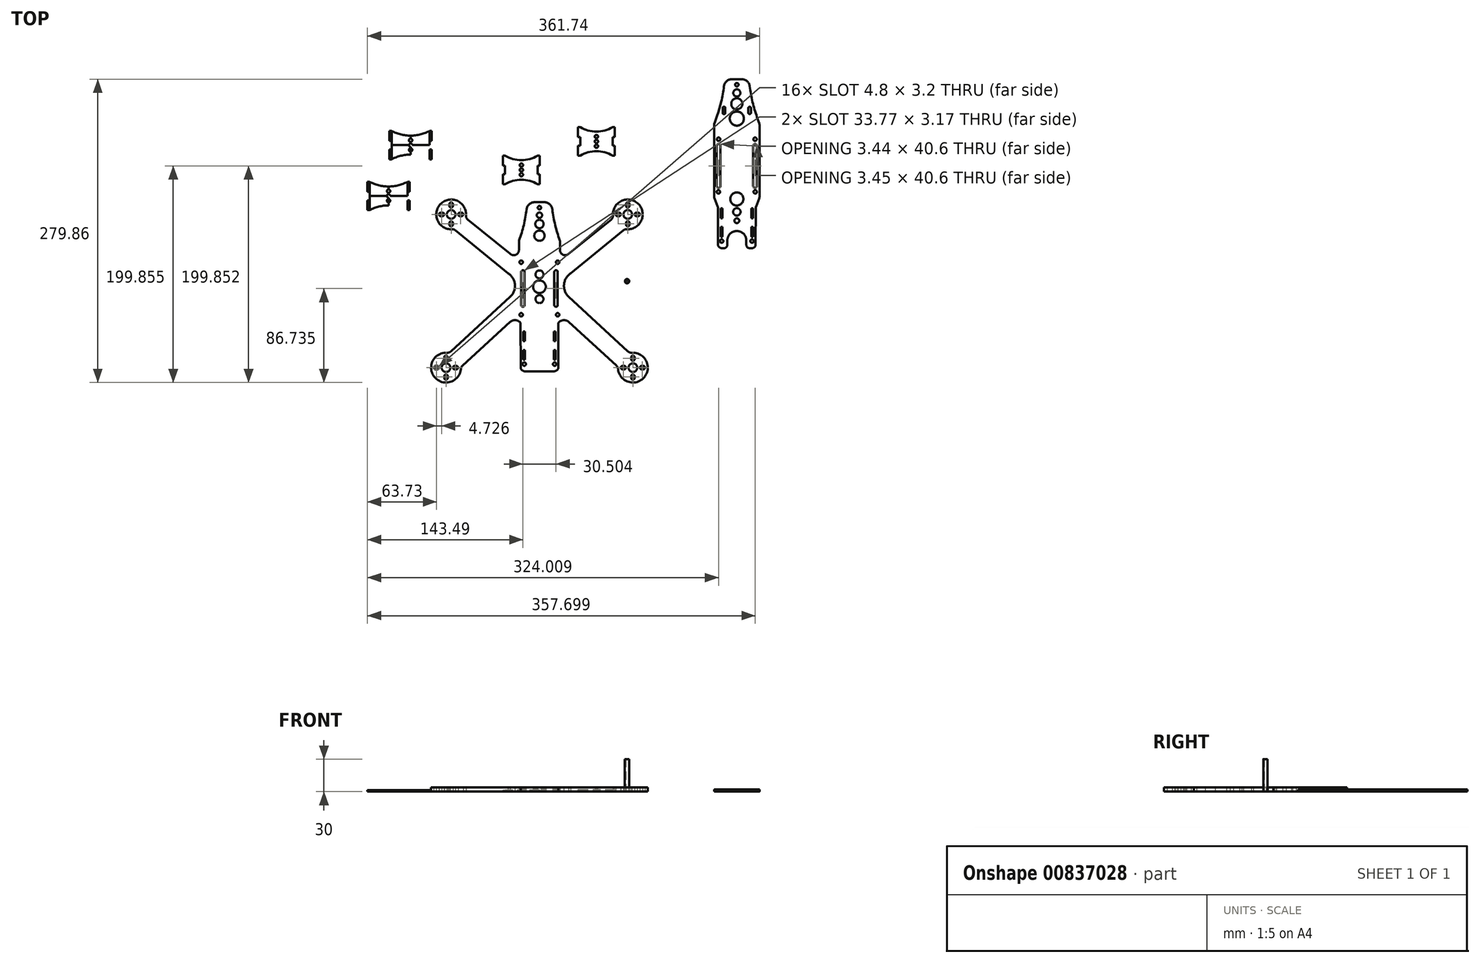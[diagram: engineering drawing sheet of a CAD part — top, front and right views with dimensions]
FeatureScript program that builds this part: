
annotation { "Feature Type Name" : "Feature", "Feature Type Description" : "" }
export const myFeature = defineFeature(function(context is Context, id is Id, definition is map)
    precondition{}
    {
        {
            var Q0;
            Q0=qCreatedBy(makeId("Top.planeOp"),FACE);
            var sketch = newSketch(context, id + "F0", { "sketchPlane" : qUnion([Q0])});
            skLineSegment(sketch, "E0.bottom", {"start": v(-59.9, 57.88) * mm, "end": v(-57.9, 57.88) * mm});
            skLineSegment(sketch, "E0.top", {"start": v(-59.9, 48.78) * mm, "end": v(-57.9, 48.78) * mm});
            skLineSegment(sketch, "E0.left", {"start": v(-59.9, 57.88) * mm, "end": v(-59.9, 48.78) * mm});
            skLineSegment(sketch, "E0.right", {"start": v(-57.9, 57.88) * mm, "end": v(-57.9, 48.78) * mm});
            skLineSegment(sketch, "E1", {"start": v(-57.9, 48.78) * mm, "end": v(-57.9, 40.77) * mm});
            skLineSegment(sketch, "E2.top", {"start": v(-59.9, 31.67) * mm, "end": v(-57.9, 31.67) * mm});
            skLineSegment(sketch, "E2.right", {"start": v(-57.9, 40.77) * mm, "end": v(-57.9, 31.67) * mm});
            skLineSegment(sketch, "E3.left", {"start": v(-57.9, 57.88) * mm, "end": v(-57.9, 31.68) * mm});
            skArc(sketch, "E4", {"start": v(-42.9, 50.83) * mm, "mid": v(-44.47, 49.27) * mm, "end": v(-42.9, 47.7) * mm});
            skArc(sketch, "E5", {"start": v(-42.9, 41.96) * mm, "mid": v(-44.47, 40.4) * mm, "end": v(-42.9, 38.84) * mm});
            skArc(sketch, "E6", {"start": v(-42.9, 46.34) * mm, "mid": v(-44.47, 44.78) * mm, "end": v(-42.9, 43.21) * mm});
            skLineSegment(sketch, "E7", {"start": v(-42.9, 53.68) * mm, "end": v(-42.9, 35.87) * mm});
            skPoint(sketch, "E3.right.end.orphan", {"position": v(-27.9, 31.68) * mm});
            skPoint(sketch, "E8.orphan", {"position": v(-27.9, 57.88) * mm});
            skPoint(sketch, "E9.0.midPoint", {"position": v(-51.12, 49.58) * mm});
            skPoint(sketch, "E10.0.midPoint", {"position": v(-51.12, 33.98) * mm});
            skPoint(sketch, "E11.0.midPoint", {"position": v(-50.1, 42.53) * mm});
            skLineSegment(sketch, "E12.MirrorCS", {"start": v(-27.9, 57.88) * mm, "end": v(-27.9, 48.78) * mm});
            skLineSegment(sketch, "E13.MirrorCS", {"start": v(-27.9, 40.77) * mm, "end": v(-27.9, 31.67) * mm});
            skLineSegment(sketch, "E14.MirrorCS", {"start": v(-27.9, 48.78) * mm, "end": v(-27.9, 40.77) * mm});
            skLineSegment(sketch, "E15.MirrorCS", {"start": v(-25.9, 40.77) * mm, "end": v(-25.9, 31.67) * mm});
            skLineSegment(sketch, "E16.MirrorCS", {"start": v(-25.9, 48.78) * mm, "end": v(-27.9, 48.78) * mm});
            skLineSegment(sketch, "E17.MirrorCS", {"start": v(-25.9, 57.88) * mm, "end": v(-25.9, 48.78) * mm});
            skLineSegment(sketch, "E18.MirrorCS", {"start": v(-27.9, 57.88) * mm, "end": v(-27.9, 31.68) * mm});
            skArc(sketch, "E19.MirrorCS", {"start": v(-42.9, 50.83) * mm, "mid": v(-41.34, 49.27) * mm, "end": v(-42.9, 47.7) * mm});
            skLineSegment(sketch, "E20.MirrorCS", {"start": v(-25.9, 31.67) * mm, "end": v(-27.9, 31.67) * mm});
            skLineSegment(sketch, "E21.MirrorCS", {"start": v(-25.9, 57.88) * mm, "end": v(-27.9, 57.88) * mm});
            skLineSegment(sketch, "E22.MirrorCS", {"start": v(-25.9, 40.77) * mm, "end": v(-27.9, 40.77) * mm});
            skArc(sketch, "E23.MirrorCS", {"start": v(-42.9, 46.34) * mm, "mid": v(-41.34, 44.78) * mm, "end": v(-42.9, 43.21) * mm});
            skArc(sketch, "E24.MirrorCS", {"start": v(-42.9, 41.96) * mm, "mid": v(-41.34, 40.4) * mm, "end": v(-42.9, 38.84) * mm});
            skLineSegment(sketch, "E25", {"start": v(-57.9, 40.77) * mm, "end": v(-59.9, 40.77) * mm});
            skLineSegment(sketch, "E26", {"start": v(-59.9, 40.77) * mm, "end": v(-59.9, 31.67) * mm});
            skLineSegment(sketch, "E27", {"start": v(-59.9, 31.67) * mm, "end": v(-57.9, 31.68) * mm});
            skPoint(sketch, "E28.orphan", {"position": v(-59.9, 31.67) * mm});
            skPoint(sketch, "E29.orphan", {"position": v(-42.9, 57.88) * mm});
            skPoint(sketch, "E30.orphan", {"position": v(-42.9, 31.68) * mm});
            skArc(sketch, "E31", {"start": v(-57.9, 57.88) * mm, "mid": v(-42.9, 53.84) * mm, "end": v(-27.9, 57.88) * mm});
            skLineSegment(sketch, "E32", {"start": v(-57.9, 44.78) * mm, "end": v(-27.9, 44.78) * mm});
            skArc(sketch, "E33.MirrorCS", {"start": v(-57.9, 31.68) * mm, "mid": v(-42.9, 35.71) * mm, "end": v(-27.9, 31.68) * mm});
            skSolve(sketch);
        }
        {
            var Q0;
            Q0=qCreatedBy(makeId("Top.planeOp"),FACE);
            var sketch = newSketch(context, id + "F1", { "sketchPlane" : qUnion([Q0])});
            skLineSegment(sketch, "E34.MirrorCS", {"start": v(0.83, -72.32) * mm, "end": v(55.44, -122.6) * mm});
            skLineSegment(sketch, "E35.MirrorCS", {"start": v(0.73, -95.48) * mm, "end": v(44.7, -135.8) * mm});
            skLineSegment(sketch, "E36.MirrorCS", {"start": v(2.74, -50.53) * mm, "end": v(51.32, -10.9) * mm});
            skLineSegment(sketch, "E37.MirrorCS", {"start": v(0.34, -32.94) * mm, "end": v(39.96, -0.95) * mm});
            skArc(sketch, "E38.MirrorCS", {"start": v(-21.66, 7.63) * mm, "mid": v(-21.66, 7.63) * mm, "end": v(-21.66, 7.63) * mm});
            skLineSegment(sketch, "E39", {"start": v(-26.23, 15) * mm, "end": v(-21.66, 15) * mm});
            skArc(sketch, "E40", {"start": v(-14.34, 8.5) * mm, "mid": v(-11.75, -6.01) * mm, "end": v(-7.5, -20.12) * mm});
            skArc(sketch, "E41.filletArc", {"start": v(-14.34, 8.5) * mm, "mid": v(-16.76, 13.14) * mm, "end": v(-21.66, 15) * mm});
            skPoint(sketch, "E42.MirrorP", {"position": v(-21.88, 15) * mm});
            skArc(sketch, "E43", {"start": v(-26.23, 8.41) * mm, "mid": v(-24.64, 10) * mm, "end": v(-26.23, 11.59) * mm});
            skArc(sketch, "E44", {"start": v(46.3, -138.99) * mm, "mid": v(70.46, -146.54) * mm, "end": v(59.14, -123.9) * mm});
            skPoint(sketch, "E45.visualSharp", {"position": v(41.88, 0.6) * mm});
            skPoint(sketch, "E46.visualSharp", {"position": v(-3.83, -55.9) * mm});
            skPoint(sketch, "E47.visualSharp", {"position": v(-3.86, -68) * mm});
            skPoint(sketch, "E48.visualSharp", {"position": v(57.16, -124.17) * mm});
            skArc(sketch, "E48.filletArc", {"start": v(55.44, -122.6) * mm, "mid": v(57.16, -123.63) * mm, "end": v(59.14, -123.9) * mm});
            skArc(sketch, "E49.filletArc", {"start": v(46.3, -138.99) * mm, "mid": v(45.8, -137.25) * mm, "end": v(44.7, -135.8) * mm});
            skLineSegment(sketch, "E50.MirrorCS", {"start": v(-26.23, 15) * mm, "end": v(-21.88, 15) * mm});
            skArc(sketch, "E51.MirrorCS", {"start": v(-30.58, 7.63) * mm, "mid": v(-30.58, 7.63) * mm, "end": v(-30.58, 7.63) * mm});
            skArc(sketch, "E52.MirrorC", {"start": v(-26.23, 11.59) * mm, "mid": v(-24.64, 10) * mm, "end": v(-26.23, 8.41) * mm});
            skPoint(sketch, "E53.MirrorP", {"position": v(-21.88, 7.63) * mm});
            skLineSegment(sketch, "E54", {"start": v(-26.23, -141) * mm, "end": v(-12.9, -141) * mm});
            skPoint(sketch, "E55.visualSharp", {"position": v(-4.15, -141) * mm});
            skCircle(sketch, "E56", {"center": v(-12.2, -134.36) * mm, "radius": 1.59 * mm});
            skPoint(sketch, "E57.visualSharp", {"position": v(-4.15, -91) * mm});
            skPoint(sketch, "E58.visualSharp", {"position": v(-3.84, -36.32) * mm});
            skArc(sketch, "E59", {"start": v(-9.4, -49.46) * mm, "mid": v(-10.98, -47.76) * mm, "end": v(-12.56, -49.46) * mm});
            skArc(sketch, "E60.MirrorC", {"start": v(-9.4, -79.95) * mm, "mid": v(-11.04, -81.53) * mm, "end": v(-12.56, -79.83) * mm});
            skLineSegment(sketch, "E61", {"start": v(-12.56, -49.23) * mm, "end": v(-12.56, -79.95) * mm});
            skLineSegment(sketch, "E62", {"start": v(-9.4, -49.23) * mm, "end": v(-9.4, -79.95) * mm});
            skPoint(sketch, "E63.endSnap0", {"position": v(-12.56, -64.59) * mm});
            skArc(sketch, "E64", {"start": v(54.34, -9.93) * mm, "mid": v(64.94, 13.55) * mm, "end": v(41.55, 2.74) * mm});
            skLineSegment(sketch, "E65.MirrorCS", {"start": v(93.25, 33.71) * mm, "end": v(93.25, 32.11) * mm});
            skLineSegment(sketch, "E66.MirrorCS", {"start": v(51.98, -136.03) * mm, "end": v(50.38, -136.03) * mm});
            skArc(sketch, "E67.MirrorCS", {"start": v(51.98, -136.03) * mm, "mid": v(53.58, -137.63) * mm, "end": v(51.98, -139.23) * mm});
            skArc(sketch, "E68.MirrorCS", {"start": v(50.38, -139.23) * mm, "mid": v(48.78, -137.63) * mm, "end": v(50.38, -136.03) * mm});
            skArc(sketch, "E69.MirrorCS", {"start": v(61.58, -129.73) * mm, "mid": v(59.98, -131.33) * mm, "end": v(58.38, -129.73) * mm});
            skLineSegment(sketch, "E70.MirrorCS", {"start": v(61.58, -128.13) * mm, "end": v(61.58, -129.73) * mm});
            skLineSegment(sketch, "E71.MirrorCS", {"start": v(58.38, -128.13) * mm, "end": v(58.38, -129.73) * mm});
            skArc(sketch, "E72.MirrorCS", {"start": v(58.38, -128.13) * mm, "mid": v(59.98, -126.53) * mm, "end": v(61.58, -128.13) * mm});
            skLineSegment(sketch, "E73.MirrorCS", {"start": v(51.98, -139.23) * mm, "end": v(50.38, -139.23) * mm});
            skArc(sketch, "E74.MirrorCS", {"start": v(58.38, -145.53) * mm, "mid": v(59.98, -143.93) * mm, "end": v(61.58, -145.53) * mm});
            skLineSegment(sketch, "E75.MirrorCS", {"start": v(58.38, -147.13) * mm, "end": v(58.38, -145.53) * mm});
            skArc(sketch, "E76.MirrorCS", {"start": v(61.58, -147.13) * mm, "mid": v(59.98, -148.73) * mm, "end": v(58.38, -147.13) * mm});
            skLineSegment(sketch, "E77.MirrorCS", {"start": v(61.58, -145.53) * mm, "end": v(61.58, -147.13) * mm});
            skCircle(sketch, "E78.MirrorC", {"center": v(59.98, -137.63) * mm, "radius": 4 * mm});
            skLineSegment(sketch, "E79.MirrorCS", {"start": v(69.58, -136.03) * mm, "end": v(67.98, -136.03) * mm});
            skArc(sketch, "E80.MirrorCS", {"start": v(67.98, -139.23) * mm, "mid": v(66.38, -137.63) * mm, "end": v(67.98, -136.03) * mm});
            skLineSegment(sketch, "E81.MirrorCS", {"start": v(67.98, -139.23) * mm, "end": v(69.58, -139.23) * mm});
            skArc(sketch, "E82.MirrorCS", {"start": v(69.58, -136.03) * mm, "mid": v(71.18, -137.63) * mm, "end": v(69.58, -139.23) * mm});
            skLineSegment(sketch, "E83.MirrorCS", {"start": v(47.26, 5.39) * mm, "end": v(45.66, 5.39) * mm});
            skArc(sketch, "E84.MirrorCS", {"start": v(47.26, 5.39) * mm, "mid": v(48.86, 3.79) * mm, "end": v(47.26, 2.19) * mm});
            skArc(sketch, "E85.MirrorCS", {"start": v(45.66, 2.19) * mm, "mid": v(44.06, 3.79) * mm, "end": v(45.66, 5.39) * mm});
            skArc(sketch, "E86.MirrorCS", {"start": v(56.86, 11.69) * mm, "mid": v(55.26, 10.09) * mm, "end": v(53.66, 11.69) * mm});
            skLineSegment(sketch, "E87.MirrorCS", {"start": v(56.86, 13.29) * mm, "end": v(56.86, 11.69) * mm});
            skLineSegment(sketch, "E88.MirrorCS", {"start": v(53.66, 13.29) * mm, "end": v(53.66, 11.69) * mm});
            skArc(sketch, "E89.MirrorCS", {"start": v(53.66, 13.29) * mm, "mid": v(55.26, 14.89) * mm, "end": v(56.86, 13.29) * mm});
            skLineSegment(sketch, "E90.MirrorCS", {"start": v(47.26, 2.19) * mm, "end": v(45.66, 2.19) * mm});
            skArc(sketch, "E91.MirrorCS", {"start": v(53.66, -4.11) * mm, "mid": v(55.26, -2.51) * mm, "end": v(56.86, -4.11) * mm});
            skLineSegment(sketch, "E92.MirrorCS", {"start": v(53.66, -5.71) * mm, "end": v(53.66, -4.11) * mm});
            skArc(sketch, "E93.MirrorCS", {"start": v(56.86, -5.71) * mm, "mid": v(55.26, -7.31) * mm, "end": v(53.66, -5.71) * mm});
            skLineSegment(sketch, "E94.MirrorCS", {"start": v(56.86, -4.11) * mm, "end": v(56.86, -5.71) * mm});
            skCircle(sketch, "E95.MirrorC", {"center": v(55.26, 3.79) * mm, "radius": 4 * mm});
            skLineSegment(sketch, "E96.MirrorCS", {"start": v(64.86, 5.39) * mm, "end": v(63.26, 5.39) * mm});
            skArc(sketch, "E97.MirrorCS", {"start": v(63.26, 2.19) * mm, "mid": v(61.66, 3.79) * mm, "end": v(63.26, 5.39) * mm});
            skLineSegment(sketch, "E98.MirrorCS", {"start": v(63.26, 2.19) * mm, "end": v(64.86, 2.19) * mm});
            skArc(sketch, "E99.MirrorCS", {"start": v(64.86, 5.39) * mm, "mid": v(66.46, 3.79) * mm, "end": v(64.86, 2.19) * mm});
            skPoint(sketch, "E100.orphan", {"position": v(-4.2, -107.89) * mm});
            skPoint(sketch, "E101.visualSharp", {"position": v(-10.15, -141) * mm});
            skArc(sketch, "E101.filletArc", {"start": v(-12.9, -141) * mm, "mid": v(-10.54, -140.3) * mm, "end": v(-8.94, -138.43) * mm});
            skPoint(sketch, "E102.visualSharp", {"position": v(52.75, -9.73) * mm});
            skArc(sketch, "E102.filletArc", {"start": v(54.34, -9.93) * mm, "mid": v(52.74, -10.13) * mm, "end": v(51.32, -10.9) * mm});
            skArc(sketch, "E103.filletArc", {"start": v(39.96, -0.95) * mm, "mid": v(41.2, 0.7) * mm, "end": v(41.55, 2.74) * mm});
            skLineSegment(sketch, "E104", {"start": v(-8.73, -96.45) * mm, "end": v(-8.94, -138.43) * mm});
            skArc(sketch, "E105", {"start": v(0.73, -95.48) * mm, "mid": v(-4.13, -93.82) * mm, "end": v(-8.66, -96.25) * mm});
            skLineSegment(sketch, "E106", {"start": v(-7.31, -21.23) * mm, "end": v(-7.31, -29.47) * mm});
            skPoint(sketch, "E107.orphan", {"position": v(-3.73, -29.32) * mm});
            skPoint(sketch, "E108.visualSharp", {"position": v(-7.31, -34.27) * mm});
            skPoint(sketch, "E109.visualSharp", {"position": v(-1.3, -34.27) * mm});
            skPoint(sketch, "E110.MirrorCS.end.orphan", {"position": v(-12.56, -87.45) * mm});
            skPoint(sketch, "E110.MirrorCS.start.orphan", {"position": v(-12.56, -79.83) * mm});
            skPoint(sketch, "E111.visualSharp", {"position": v(1.83, -51.27) * mm});
            skPoint(sketch, "E112.visualSharp", {"position": v(-7.31, -20.65) * mm});
            skArc(sketch, "E112.filletArc", {"start": v(-7.31, -21.23) * mm, "mid": v(-7.36, -20.67) * mm, "end": v(-7.5, -20.12) * mm});
            skArc(sketch, "E113.MirrorCS", {"start": v(0.83, -72.32) * mm, "mid": v(-3.57, -60.95) * mm, "end": v(2.74, -50.53) * mm});
            skCircle(sketch, "E114.MirrorC", {"center": v(-9.4, -88.84) * mm, "radius": 1.59 * mm});
            skCircle(sketch, "E115.MirrorC", {"center": v(-9.4, -40.34) * mm, "radius": 1.59 * mm});
            skArc(sketch, "E116", {"start": v(-26.23, -55.28) * mm, "mid": v(-22.54, -51.6) * mm, "end": v(-26.23, -47.91) * mm});
            skArc(sketch, "E117", {"start": v(-26.23, -68.87) * mm, "mid": v(-20.36, -63) * mm, "end": v(-26.23, -57.13) * mm});
            skArc(sketch, "E118.MirrorC", {"start": v(-26.23, -70.72) * mm, "mid": v(-22.54, -74.4) * mm, "end": v(-26.23, -78.09) * mm});
            skPoint(sketch, "E119.visualSharp", {"position": v(-23.79, 5.4) * mm});
            skArc(sketch, "E120", {"start": v(-26.23, 0.55) * mm, "mid": v(-23.74, 3.04) * mm, "end": v(-26.23, 5.52) * mm});
            skArc(sketch, "E121", {"start": v(-26.23, -9) * mm, "mid": v(-22.35, -5.11) * mm, "end": v(-26.23, -1.23) * mm});
            skArc(sketch, "E122", {"start": v(-26.23, -20.63) * mm, "mid": v(-21.47, -15.87) * mm, "end": v(-26.23, -11.12) * mm});
            skArc(sketch, "E123", {"start": v(-7.31, -29.47) * mm, "mid": v(-4.29, -33.53) * mm, "end": v(0.7, -32.65) * mm});
            skLineSegment(sketch, "E124.MirrorCS", {"start": v(-99.71, 2.19) * mm, "end": v(-98.11, 2.19) * mm});
            skLineSegment(sketch, "E125.MirrorCS", {"start": v(-99.71, 5.39) * mm, "end": v(-98.11, 5.39) * mm});
            skArc(sketch, "E126.MirrorCS", {"start": v(-92.41, -0.95) * mm, "mid": v(-93.66, 0.7) * mm, "end": v(-94, 2.74) * mm});
            skArc(sketch, "E127.MirrorCS", {"start": v(-98.11, 2.19) * mm, "mid": v(-96.51, 3.79) * mm, "end": v(-98.11, 5.39) * mm});
            skLineSegment(sketch, "E128.MirrorCS", {"start": v(-106.11, -5.71) * mm, "end": v(-106.11, -4.11) * mm});
            skArc(sketch, "E129.MirrorCS", {"start": v(-99.71, 5.39) * mm, "mid": v(-101.31, 3.79) * mm, "end": v(-99.71, 2.19) * mm});
            skLineSegment(sketch, "E130.MirrorCS", {"start": v(-110.84, -128.13) * mm, "end": v(-110.84, -129.73) * mm});
            skLineSegment(sketch, "E131.MirrorCS", {"start": v(-41.1, -130.4) * mm, "end": v(-39.5, -130.4) * mm});
            skArc(sketch, "E132.MirrorCS", {"start": v(-114.04, -129.73) * mm, "mid": v(-112.44, -131.33) * mm, "end": v(-110.84, -129.73) * mm});
            skLineSegment(sketch, "E133.MirrorCS", {"start": v(-26.23, 15) * mm, "end": v(-30.8, 15) * mm});
            skLineSegment(sketch, "E134.MirrorCS", {"start": v(-122.04, -136.03) * mm, "end": v(-120.44, -136.03) * mm});
            skArc(sketch, "E135.MirrorCS", {"start": v(-110.84, -128.13) * mm, "mid": v(-112.44, -126.53) * mm, "end": v(-114.04, -128.13) * mm});
            skLineSegment(sketch, "E136.MirrorCS", {"start": v(-109.31, -4.11) * mm, "end": v(-109.31, -5.71) * mm});
            skArc(sketch, "E137.MirrorCS", {"start": v(-26.23, 11.59) * mm, "mid": v(-27.81, 10) * mm, "end": v(-26.23, 8.41) * mm});
            skArc(sketch, "E138.MirrorCS", {"start": v(-107.9, -122.6) * mm, "mid": v(-109.61, -123.63) * mm, "end": v(-111.6, -123.9) * mm});
            skLineSegment(sketch, "E139.MirrorCS", {"start": v(-115.71, 2.19) * mm, "end": v(-117.31, 2.19) * mm});
            skLineSegment(sketch, "E140.MirrorCS", {"start": v(-117.31, 5.39) * mm, "end": v(-115.71, 5.39) * mm});
            skLineSegment(sketch, "E141.MirrorCS", {"start": v(-114.04, -128.13) * mm, "end": v(-114.04, -129.73) * mm});
            skArc(sketch, "E142.MirrorCS", {"start": v(-106.11, -4.11) * mm, "mid": v(-107.71, -2.51) * mm, "end": v(-109.31, -4.11) * mm});
            skCircle(sketch, "E143.MirrorC", {"center": v(-40.25, -134.36) * mm, "radius": 1.59 * mm});
            skArc(sketch, "E144.MirrorCS", {"start": v(-115.71, 2.19) * mm, "mid": v(-114.11, 3.79) * mm, "end": v(-115.71, 5.39) * mm});
            skLineSegment(sketch, "E145.MirrorCS", {"start": v(-114.04, -145.53) * mm, "end": v(-114.04, -147.13) * mm});
            skArc(sketch, "E146.MirrorCS", {"start": v(-120.44, -139.23) * mm, "mid": v(-118.84, -137.63) * mm, "end": v(-120.44, -136.03) * mm});
            skLineSegment(sketch, "E147.MirrorCS", {"start": v(-41.1, -113.28) * mm, "end": v(-41.1, -104.16) * mm});
            skArc(sketch, "E148.MirrorCS", {"start": v(-26.23, 8.41) * mm, "mid": v(-27.81, 10) * mm, "end": v(-26.23, 11.59) * mm});
            skArc(sketch, "E149.MirrorCS", {"start": v(-104.44, -136.03) * mm, "mid": v(-106.04, -137.63) * mm, "end": v(-104.44, -139.23) * mm});
            skLineSegment(sketch, "E150.MirrorCS", {"start": v(-41.1, -121.28) * mm, "end": v(-39.5, -121.28) * mm});
            skLineSegment(sketch, "E151.MirrorCS", {"start": v(-26.23, 15) * mm, "end": v(-30.58, 15) * mm});
            skLineSegment(sketch, "E152.MirrorCS", {"start": v(-41.1, -121.28) * mm, "end": v(-41.1, -130.4) * mm});
            skArc(sketch, "E153.MirrorCS", {"start": v(-114.04, -147.13) * mm, "mid": v(-112.44, -148.73) * mm, "end": v(-110.84, -147.13) * mm});
            skArc(sketch, "E154.MirrorCS", {"start": v(-30.8, 7.63) * mm, "mid": v(-30.8, 7.63) * mm, "end": v(-30.8, 7.63) * mm});
            skLineSegment(sketch, "E155.MirrorCS", {"start": v(-110.84, -147.13) * mm, "end": v(-110.84, -145.53) * mm});
            skArc(sketch, "E156.MirrorCS", {"start": v(-21.88, 7.63) * mm, "mid": v(-21.88, 7.63) * mm, "end": v(-21.88, 7.63) * mm});
            skLineSegment(sketch, "E157.MirrorCS", {"start": v(-41.1, -113.28) * mm, "end": v(-39.5, -113.28) * mm});
            skArc(sketch, "E158.MirrorCS", {"start": v(-38.12, 8.5) * mm, "mid": v(-35.7, 13.14) * mm, "end": v(-30.8, 15) * mm});
            skLineSegment(sketch, "E159.MirrorCS", {"start": v(-39.5, -121.28) * mm, "end": v(-39.5, -130.4) * mm});
            skCircle(sketch, "E160.MirrorC", {"center": v(-112.44, -137.63) * mm, "radius": 4 * mm});
            skArc(sketch, "E161.MirrorCS", {"start": v(-110.84, -145.53) * mm, "mid": v(-112.44, -143.93) * mm, "end": v(-114.04, -145.53) * mm});
            skArc(sketch, "E162.MirrorCS", {"start": v(-45.14, -21.23) * mm, "mid": v(-45.1, -20.67) * mm, "end": v(-44.95, -20.12) * mm});
            skCircle(sketch, "E163.MirrorC", {"center": v(-107.71, 3.79) * mm, "radius": 4 * mm});
            skLineSegment(sketch, "E164.MirrorCS", {"start": v(-120.44, -139.23) * mm, "end": v(-122.04, -139.23) * mm});
            skLineSegment(sketch, "E165.MirrorCS", {"start": v(-104.44, -136.03) * mm, "end": v(-102.84, -136.03) * mm});
            skArc(sketch, "E166.MirrorCS", {"start": v(-117.31, 5.39) * mm, "mid": v(-118.91, 3.79) * mm, "end": v(-117.31, 2.19) * mm});
            skArc(sketch, "E167.MirrorCS", {"start": v(-102.84, -139.23) * mm, "mid": v(-101.24, -137.63) * mm, "end": v(-102.84, -136.03) * mm});
            skLineSegment(sketch, "E168.MirrorCS", {"start": v(-39.5, -113.28) * mm, "end": v(-39.5, -104.16) * mm});
            skLineSegment(sketch, "E169.MirrorCS", {"start": v(-109.31, 13.29) * mm, "end": v(-109.31, 11.69) * mm});
            skLineSegment(sketch, "E170.MirrorCS", {"start": v(-104.44, -139.23) * mm, "end": v(-102.84, -139.23) * mm});
            skLineSegment(sketch, "E171.MirrorCS", {"start": v(-43.73, -96.45) * mm, "end": v(-43.51, -138.43) * mm});
            skArc(sketch, "E172.MirrorCS", {"start": v(-98.76, -138.99) * mm, "mid": v(-98.25, -137.25) * mm, "end": v(-97.16, -135.8) * mm});
            skArc(sketch, "E173.MirrorCS", {"start": v(-109.31, 11.69) * mm, "mid": v(-107.71, 10.09) * mm, "end": v(-106.11, 11.69) * mm});
            skArc(sketch, "E174.MirrorCS", {"start": v(-26.23, 0.55) * mm, "mid": v(-28.71, 3.04) * mm, "end": v(-26.23, 5.52) * mm});
            skLineSegment(sketch, "E175.MirrorCS", {"start": v(-41.1, -104.16) * mm, "end": v(-39.5, -104.16) * mm});
            skArc(sketch, "E176.MirrorCS", {"start": v(-43.06, -49.46) * mm, "mid": v(-41.48, -47.76) * mm, "end": v(-39.9, -49.46) * mm});
            skArc(sketch, "E177.MirrorCS", {"start": v(-26.23, -9) * mm, "mid": v(-30.1, -5.11) * mm, "end": v(-26.23, -1.23) * mm});
            skArc(sketch, "E178.MirrorCS", {"start": v(-43.06, -79.95) * mm, "mid": v(-41.42, -81.53) * mm, "end": v(-39.9, -79.83) * mm});
            skArc(sketch, "E179.MirrorCS", {"start": v(-109.31, -5.71) * mm, "mid": v(-107.71, -7.31) * mm, "end": v(-106.11, -5.71) * mm});
            skArc(sketch, "E180.MirrorCS", {"start": v(-45.14, -29.47) * mm, "mid": v(-48.17, -33.53) * mm, "end": v(-53.16, -32.65) * mm});
            skArc(sketch, "E181.MirrorCS", {"start": v(-39.56, -141) * mm, "mid": v(-41.92, -140.3) * mm, "end": v(-43.51, -138.43) * mm});
            skArc(sketch, "E182.MirrorCS", {"start": v(-106.11, 13.29) * mm, "mid": v(-107.71, 14.89) * mm, "end": v(-109.31, 13.29) * mm});
            skLineSegment(sketch, "E183.MirrorCS", {"start": v(-106.11, 13.29) * mm, "end": v(-106.11, 11.69) * mm});
            skLineSegment(sketch, "E184.MirrorCS", {"start": v(-45.14, -21.23) * mm, "end": v(-45.14, -29.47) * mm});
            skLineSegment(sketch, "E185.MirrorCS", {"start": v(-26.23, -141) * mm, "end": v(-39.56, -141) * mm});
            skArc(sketch, "E186.MirrorCS", {"start": v(-106.8, -9.93) * mm, "mid": v(-105.2, -10.13) * mm, "end": v(-103.78, -10.9) * mm});
            skCircle(sketch, "E187.MirrorC", {"center": v(-43.06, -88.84) * mm, "radius": 1.59 * mm});
            skArc(sketch, "E188.MirrorCS", {"start": v(-98.76, -138.99) * mm, "mid": v(-122.91, -146.54) * mm, "end": v(-111.6, -123.9) * mm});
            skArc(sketch, "E189.MirrorCS", {"start": v(-122.04, -136.03) * mm, "mid": v(-123.64, -137.63) * mm, "end": v(-122.04, -139.23) * mm});
            skArc(sketch, "E190.MirrorCS", {"start": v(-26.23, -55.28) * mm, "mid": v(-29.91, -51.6) * mm, "end": v(-26.23, -47.91) * mm});
            skCircle(sketch, "E191.MirrorC", {"center": v(-43.06, -40.34) * mm, "radius": 1.59 * mm});
            skArc(sketch, "E192.MirrorCS", {"start": v(-26.23, -70.72) * mm, "mid": v(-29.91, -74.4) * mm, "end": v(-26.23, -78.09) * mm});
            skArc(sketch, "E193.MirrorCS", {"start": v(-26.23, -68.87) * mm, "mid": v(-32.1, -63) * mm, "end": v(-26.23, -57.13) * mm});
            skPoint(sketch, "E194.MirrorP", {"position": v(-30.58, 15) * mm});
            skArc(sketch, "E195.MirrorCS", {"start": v(-53.19, -95.48) * mm, "mid": v(-48.33, -93.82) * mm, "end": v(-43.8, -96.25) * mm});
            skPoint(sketch, "E196.MirrorP", {"position": v(-94.34, 0.6) * mm});
            skArc(sketch, "E197.MirrorCS", {"start": v(-26.23, -20.63) * mm, "mid": v(-30.98, -15.87) * mm, "end": v(-26.23, -11.12) * mm});
            skPoint(sketch, "E198.MirrorP", {"position": v(-42.3, -141) * mm});
            skPoint(sketch, "E199.MirrorP", {"position": v(-48.3, -141) * mm});
            skArc(sketch, "E200.MirrorCS", {"start": v(-53.29, -72.32) * mm, "mid": v(-48.88, -60.95) * mm, "end": v(-55.2, -50.53) * mm});
            skPoint(sketch, "E201.MirrorP", {"position": v(-30.58, 7.63) * mm});
            skPoint(sketch, "E202.MirrorP", {"position": v(-45.14, -20.65) * mm});
            skArc(sketch, "E203.MirrorCS", {"start": v(-38.12, 8.5) * mm, "mid": v(-40.7, -6.01) * mm, "end": v(-44.95, -20.12) * mm});
            skLineSegment(sketch, "E204.MirrorCS", {"start": v(-43.06, -49.23) * mm, "end": v(-43.06, -79.95) * mm});
            skLineSegment(sketch, "E205.MirrorCS", {"start": v(-39.9, -49.23) * mm, "end": v(-39.9, -79.95) * mm});
            skPoint(sketch, "E206.MirrorP", {"position": v(-48.73, -29.32) * mm});
            skPoint(sketch, "E207.MirrorP", {"position": v(-28.67, 5.4) * mm});
            skPoint(sketch, "E208.MirrorP", {"position": v(-51.15, -34.27) * mm});
            skLineSegment(sketch, "E209.MirrorCS", {"start": v(-55.2, -50.53) * mm, "end": v(-103.78, -10.9) * mm});
            skPoint(sketch, "E210.MirrorP", {"position": v(-105.2, -9.73) * mm});
            skPoint(sketch, "E211.MirrorP", {"position": v(-39.9, -64.59) * mm});
            skPoint(sketch, "E212.MirrorP", {"position": v(-54.28, -51.27) * mm});
            skPoint(sketch, "E213.MirrorP", {"position": v(-48.61, -36.32) * mm});
            skPoint(sketch, "E214.MirrorP", {"position": v(-45.14, -34.27) * mm});
            skLineSegment(sketch, "E215.MirrorCS", {"start": v(-53.19, -95.48) * mm, "end": v(-97.16, -135.8) * mm});
            skLineSegment(sketch, "E216.MirrorCS", {"start": v(-53.29, -72.32) * mm, "end": v(-107.9, -122.6) * mm});
            skPoint(sketch, "E217.MirrorP", {"position": v(-48.25, -107.89) * mm});
            skArc(sketch, "E218.MirrorCS", {"start": v(-106.8, -9.93) * mm, "mid": v(-117.4, 13.55) * mm, "end": v(-94, 2.74) * mm});
            skPoint(sketch, "E219.MirrorP", {"position": v(-48.6, -68) * mm});
            skPoint(sketch, "E220.MirrorP", {"position": v(-48.3, -91) * mm});
            skPoint(sketch, "E221.MirrorP", {"position": v(-48.63, -55.9) * mm});
            skPoint(sketch, "E222.MirrorP", {"position": v(-39.9, -79.83) * mm});
            skPoint(sketch, "E223.MirrorP", {"position": v(-39.9, -87.45) * mm});
            skLineSegment(sketch, "E224.MirrorCS", {"start": v(-52.8, -32.94) * mm, "end": v(-92.41, -0.95) * mm});
            skPoint(sketch, "E225.MirrorP", {"position": v(-109.61, -124.17) * mm});
            skLineSegment(sketch, "E226.MirrorCS", {"start": v(-11.36, -113.28) * mm, "end": v(-12.96, -113.28) * mm});
            skLineSegment(sketch, "E227.MirrorCS", {"start": v(-11.36, -130.4) * mm, "end": v(-12.96, -130.4) * mm});
            skLineSegment(sketch, "E228.MirrorCS", {"start": v(-11.36, -121.28) * mm, "end": v(-12.96, -121.28) * mm});
            skLineSegment(sketch, "E229.MirrorCS", {"start": v(-11.36, -104.16) * mm, "end": v(-12.96, -104.16) * mm});
            skLineSegment(sketch, "E230.MirrorCS", {"start": v(-12.96, -121.28) * mm, "end": v(-12.96, -130.4) * mm});
            skLineSegment(sketch, "E231.MirrorCS", {"start": v(-11.36, -113.28) * mm, "end": v(-11.36, -104.16) * mm});
            skLineSegment(sketch, "E232.MirrorCS", {"start": v(-11.36, -121.28) * mm, "end": v(-11.36, -130.4) * mm});
            skLineSegment(sketch, "E233.MirrorCS", {"start": v(-12.96, -113.28) * mm, "end": v(-12.96, -104.16) * mm});
            skPoint(sketch, "E234.visualSharp", {"position": v(-8.73, -96.34) * mm});
            skArc(sketch, "E234.filletArc", {"start": v(-8.66, -96.25) * mm, "mid": v(-8.7, -96.34) * mm, "end": v(-8.73, -96.45) * mm});
            skPoint(sketch, "E235.visualSharp", {"position": v(-43.73, -96.34) * mm});
            skArc(sketch, "E235.filletArc", {"start": v(-43.73, -96.45) * mm, "mid": v(-43.75, -96.34) * mm, "end": v(-43.8, -96.25) * mm});
            skSolve(sketch);
        }
        {
            var Q0;
            Q0=qCreatedBy(makeId("Top.planeOp"),FACE);
            var sketch = newSketch(context, id + "F2", { "sketchPlane" : qUnion([Q0])});
            skLineSegment(sketch, "E236", {"start": v(155.88, 128.48) * mm, "end": v(160.44, 128.48) * mm});
            skPoint(sketch, "E237.start.orphan", {"position": v(151.3, 128.48) * mm});
            skPoint(sketch, "E238.MirrorP", {"position": v(160.23, 128.48) * mm});
            skArc(sketch, "E239", {"start": v(155.88, 121.89) * mm, "mid": v(157.46, 123.48) * mm, "end": v(155.88, 125.06) * mm});
            skPoint(sketch, "E240.MirrorP", {"position": v(151.53, 128.48) * mm});
            skPoint(sketch, "E241.orphan", {"position": v(139.8, -27.53) * mm});
            skLineSegment(sketch, "E242.MirrorCS", {"start": v(275.36, 147.19) * mm, "end": v(275.36, 145.59) * mm});
            skLineSegment(sketch, "E243.MirrorCS", {"start": v(155.88, 128.48) * mm, "end": v(151.3, 128.48) * mm});
            skArc(sketch, "E244.MirrorCS", {"start": v(143.99, 121.97) * mm, "mid": v(146.41, 126.62) * mm, "end": v(151.3, 128.48) * mm});
            skArc(sketch, "E245.MirrorCS", {"start": v(143.99, 121.97) * mm, "mid": v(141.44, 107.61) * mm, "end": v(137.26, 93.63) * mm});
            skArc(sketch, "E246.MirrorCS", {"start": v(155.88, 121.89) * mm, "mid": v(154.29, 123.48) * mm, "end": v(155.88, 125.06) * mm});
            skLineSegment(sketch, "E247.MirrorCS", {"start": v(141.01, -16.93) * mm, "end": v(142.61, -16.93) * mm});
            skLineSegment(sketch, "E248.MirrorCS", {"start": v(141.01, -7.8) * mm, "end": v(142.61, -7.8) * mm});
            skLineSegment(sketch, "E249.MirrorCS", {"start": v(141.01, 0.2) * mm, "end": v(142.61, 0.2) * mm});
            skCircle(sketch, "E250.MirrorC", {"center": v(141.86, -20.88) * mm, "radius": 1.59 * mm});
            skLineSegment(sketch, "E251.MirrorCS", {"start": v(141.01, -7.8) * mm, "end": v(141.01, -16.93) * mm});
            skLineSegment(sketch, "E252.MirrorCS", {"start": v(143.9, -27.53) * mm, "end": v(142.54, -27.53) * mm});
            skLineSegment(sketch, "E253.MirrorCS", {"start": v(142.61, -7.8) * mm, "end": v(142.61, -16.93) * mm});
            skLineSegment(sketch, "E254.MirrorCS", {"start": v(142.61, 0.2) * mm, "end": v(142.61, 9.32) * mm});
            skLineSegment(sketch, "E255.MirrorCS", {"start": v(141.01, 0.2) * mm, "end": v(141.01, 9.32) * mm});
            skArc(sketch, "E256.filletArc", {"start": v(138.6, -24.95) * mm, "mid": v(140.19, -26.83) * mm, "end": v(142.54, -27.53) * mm});
            skLineSegment(sketch, "E257", {"start": v(138.41, 9.95) * mm, "end": v(138.6, -24.95) * mm});
            skLineSegment(sketch, "E258", {"start": v(142.2, 33.61) * mm, "end": v(142.2, 33.38) * mm});
            skPoint(sketch, "E259.visualSharp", {"position": v(136.96, 92.82) * mm});
            skCircle(sketch, "E260", {"center": v(138.9, 24.6) * mm, "radius": 1.59 * mm});
            skCircle(sketch, "E261.MirrorC", {"center": v(139.04, 73.14) * mm, "radius": 1.59 * mm});
            skLineSegment(sketch, "E262", {"start": v(135, 86.78) * mm, "end": v(135, 19.91) * mm});
            skPoint(sketch, "E263.orphan", {"position": v(136.96, 82.42) * mm});
            skLineSegment(sketch, "E264", {"start": v(137.26, 93.63) * mm, "end": v(135.2, 87.86) * mm});
            skPoint(sketch, "E265.start.orphan", {"position": v(137.1, 88.03) * mm});
            skLineSegment(sketch, "E266", {"start": v(135.22, 18.74) * mm, "end": v(138.2, 11.1) * mm});
            skPoint(sketch, "E267.visualSharp", {"position": v(135, 19.3) * mm});
            skArc(sketch, "E267.filletArc", {"start": v(135, 19.91) * mm, "mid": v(135.06, 19.32) * mm, "end": v(135.22, 18.74) * mm});
            skPoint(sketch, "E268.visualSharp", {"position": v(138.4, 10.55) * mm});
            skArc(sketch, "E268.filletArc", {"start": v(138.41, 9.95) * mm, "mid": v(138.36, 10.54) * mm, "end": v(138.2, 11.1) * mm});
            skPoint(sketch, "E269.visualSharp", {"position": v(135, 87.33) * mm});
            skArc(sketch, "E269.filletArc", {"start": v(135.2, 87.86) * mm, "mid": v(135.05, 87.33) * mm, "end": v(135, 86.78) * mm});
            skLineSegment(sketch, "E270", {"start": v(142.54, -27.53) * mm, "end": v(143.9, -27.53) * mm});
            skArc(sketch, "E271.filletArc", {"start": v(143.9, -27.53) * mm, "mid": v(146.18, -26.58) * mm, "end": v(147.12, -24.3) * mm});
            skArc(sketch, "E272", {"start": v(140.76, 67.02) * mm, "mid": v(139.06, 68.77) * mm, "end": v(137.32, 67.05) * mm});
            skLineSegment(sketch, "E273.MirrorC", {"start": v(140.76, 33.61) * mm, "end": v(140.76, 33.61) * mm});
            skLineSegment(sketch, "E274", {"start": v(137.32, 67.05) * mm, "end": v(137.32, 33.61) * mm});
            skLineSegment(sketch, "E275", {"start": v(140.76, 67.02) * mm, "end": v(140.76, 33.61) * mm});
            skArc(sketch, "E276", {"start": v(155.88, 119.19) * mm, "mid": v(152.56, 115.87) * mm, "end": v(155.88, 112.56) * mm});
            skArc(sketch, "E277", {"start": v(155.88, 110.93) * mm, "mid": v(150.76, 105.81) * mm, "end": v(155.88, 100.69) * mm});
            skArc(sketch, "E278", {"start": v(155.88, 98.74) * mm, "mid": v(149.33, 92.18) * mm, "end": v(155.88, 85.62) * mm});
            skArc(sketch, "E279", {"start": v(145.28, 101.83) * mm, "mid": v(144.05, 103.1) * mm, "end": v(142.8, 101.86) * mm});
            skArc(sketch, "E280.MirrorC", {"start": v(145.28, 97.57) * mm, "mid": v(144.05, 96.3) * mm, "end": v(142.8, 97.54) * mm});
            skLineSegment(sketch, "E281", {"start": v(142.8, 101.86) * mm, "end": v(142.8, 97.54) * mm});
            skLineSegment(sketch, "E282", {"start": v(145.28, 101.9) * mm, "end": v(145.28, 97.57) * mm});
            skArc(sketch, "E283", {"start": v(155.89, -11.56) * mm, "mid": v(149.58, -14.23) * mm, "end": v(147.12, -20.62) * mm});
            skLineSegment(sketch, "E284", {"start": v(147.12, -20.62) * mm, "end": v(147.12, -24.3) * mm});
            skArc(sketch, "E285", {"start": v(155.89, 24.04) * mm, "mid": v(149.84, 18) * mm, "end": v(155.89, 11.95) * mm});
            skArc(sketch, "E286", {"start": v(155.89, 9.56) * mm, "mid": v(152.44, 6.12) * mm, "end": v(155.89, 2.68) * mm});
            skArc(sketch, "E287", {"start": v(155.89, 0.15) * mm, "mid": v(153.66, -2.07) * mm, "end": v(155.89, -4.3) * mm});
            skPoint(sketch, "E288.0.midPoint", {"position": v(155.88, 44.72) * mm});
            skPoint(sketch, "E289.orphan", {"position": v(152.3, 44.72) * mm});
            skLineSegment(sketch, "E290", {"start": v(137.32, 33.61) * mm, "end": v(137.32, 29.89) * mm});
            skArc(sketch, "E291", {"start": v(137.32, 29.89) * mm, "mid": v(139.04, 28.17) * mm, "end": v(140.76, 29.89) * mm});
            skLineSegment(sketch, "E292", {"start": v(140.76, 33.61) * mm, "end": v(140.76, 29.89) * mm});
            skLineSegment(sketch, "E293.MirrorCS", {"start": v(169.24, -27.52) * mm, "end": v(167.88, -27.53) * mm});
            skLineSegment(sketch, "E294.MirrorCS", {"start": v(167.88, -27.53) * mm, "end": v(169.24, -27.52) * mm});
            skArc(sketch, "E295.MirrorCS", {"start": v(173.19, -24.95) * mm, "mid": v(171.6, -26.82) * mm, "end": v(169.24, -27.52) * mm});
            skArc(sketch, "E296.MirrorCS", {"start": v(167.88, -27.53) * mm, "mid": v(165.6, -26.58) * mm, "end": v(164.66, -24.3) * mm});
            skArc(sketch, "E297.MirrorCS", {"start": v(176.77, 19.91) * mm, "mid": v(176.71, 19.32) * mm, "end": v(176.55, 18.75) * mm});
            skLineSegment(sketch, "E298.MirrorCS", {"start": v(174.45, 33.61) * mm, "end": v(174.45, 29.9) * mm});
            skArc(sketch, "E299.MirrorCS", {"start": v(174.45, 29.9) * mm, "mid": v(172.73, 28.17) * mm, "end": v(171.01, 29.9) * mm});
            skCircle(sketch, "E300.MirrorC", {"center": v(169.93, -20.88) * mm, "radius": 1.59 * mm});
            skArc(sketch, "E301.MirrorCS", {"start": v(173.36, 9.96) * mm, "mid": v(173.42, 10.54) * mm, "end": v(173.58, 11.1) * mm});
            skLineSegment(sketch, "E302.MirrorCS", {"start": v(176.55, 18.75) * mm, "end": v(173.58, 11.1) * mm});
            skLineSegment(sketch, "E303.MirrorCS", {"start": v(171.01, 33.61) * mm, "end": v(171.01, 29.9) * mm});
            skLineSegment(sketch, "E304.MirrorCS", {"start": v(169.56, 33.61) * mm, "end": v(169.56, 33.38) * mm});
            skLineSegment(sketch, "E305.MirrorCS", {"start": v(164.66, -20.62) * mm, "end": v(164.66, -24.3) * mm});
            skArc(sketch, "E306.MirrorCS", {"start": v(166.48, 101.84) * mm, "mid": v(167.7, 103.1) * mm, "end": v(168.96, 101.87) * mm});
            skLineSegment(sketch, "E307.MirrorCS", {"start": v(168.96, 101.87) * mm, "end": v(168.96, 97.54) * mm});
            skLineSegment(sketch, "E308.MirrorCS", {"start": v(174.5, 93.64) * mm, "end": v(176.57, 87.86) * mm});
            skLineSegment(sketch, "E309.MirrorCS", {"start": v(173.36, 9.96) * mm, "end": v(173.19, -24.95) * mm});
            skCircle(sketch, "E310.MirrorC", {"center": v(172.87, 24.6) * mm, "radius": 1.59 * mm});
            skArc(sketch, "E311.MirrorCS", {"start": v(171, 67.02) * mm, "mid": v(172.7, 68.78) * mm, "end": v(174.44, 67.06) * mm});
            skArc(sketch, "E312.MirrorCS", {"start": v(176.57, 87.86) * mm, "mid": v(176.7, 87.33) * mm, "end": v(176.75, 86.78) * mm});
            skArc(sketch, "E313.MirrorCS", {"start": v(166.48, 97.57) * mm, "mid": v(167.7, 96.3) * mm, "end": v(168.96, 97.54) * mm});
            skLineSegment(sketch, "E314.MirrorCS", {"start": v(166.48, 101.9) * mm, "end": v(166.48, 97.57) * mm});
            skArc(sketch, "E315.MirrorCS", {"start": v(155.88, 119.19) * mm, "mid": v(159.2, 115.87) * mm, "end": v(155.88, 112.56) * mm});
            skArc(sketch, "E316.MirrorCS", {"start": v(167.77, 121.98) * mm, "mid": v(165.34, 126.62) * mm, "end": v(160.44, 128.48) * mm});
            skArc(sketch, "E317.MirrorCS", {"start": v(155.89, 9.56) * mm, "mid": v(159.34, 6.12) * mm, "end": v(155.89, 2.68) * mm});
            skArc(sketch, "E318.MirrorCS", {"start": v(155.89, 0.15) * mm, "mid": v(158.12, -2.07) * mm, "end": v(155.89, -4.3) * mm});
            skArc(sketch, "E319.MirrorCS", {"start": v(155.88, 110.93) * mm, "mid": v(161, 105.81) * mm, "end": v(155.88, 100.69) * mm});
            skArc(sketch, "E320.MirrorCS", {"start": v(155.88, 98.74) * mm, "mid": v(162.42, 92.18) * mm, "end": v(155.88, 85.62) * mm});
            skPoint(sketch, "E321.MirrorP", {"position": v(173.37, 10.55) * mm});
            skPoint(sketch, "E322.MirrorP", {"position": v(171.98, -27.52) * mm});
            skArc(sketch, "E323.MirrorCS", {"start": v(155.89, 24.04) * mm, "mid": v(161.93, 18) * mm, "end": v(155.89, 11.95) * mm});
            skPoint(sketch, "E324.MirrorP", {"position": v(176.77, 19.31) * mm});
            skCircle(sketch, "E325.MirrorC", {"center": v(172.72, 73.14) * mm, "radius": 1.59 * mm});
            skLineSegment(sketch, "E326.MirrorCS", {"start": v(171.01, 33.61) * mm, "end": v(171.01, 33.61) * mm});
            skPoint(sketch, "E327.MirrorP", {"position": v(174.8, 82.42) * mm});
            skPoint(sketch, "E328.MirrorP", {"position": v(174.65, 88.03) * mm});
            skArc(sketch, "E329.MirrorCS", {"start": v(167.77, 121.98) * mm, "mid": v(170.32, 107.61) * mm, "end": v(174.5, 93.64) * mm});
            skLineSegment(sketch, "E330.MirrorCS", {"start": v(174.44, 67.06) * mm, "end": v(174.45, 33.61) * mm});
            skPoint(sketch, "E331.MirrorP", {"position": v(159.47, 44.72) * mm});
            skArc(sketch, "E332.MirrorCS", {"start": v(155.89, -11.56) * mm, "mid": v(162.2, -14.23) * mm, "end": v(164.66, -20.62) * mm});
            skPoint(sketch, "E333.MirrorP", {"position": v(174.8, 92.82) * mm});
            skPoint(sketch, "E334.MirrorP", {"position": v(155.9, 44.72) * mm});
            skLineSegment(sketch, "E335.MirrorCS", {"start": v(176.75, 86.78) * mm, "end": v(176.77, 19.91) * mm});
            skPoint(sketch, "E336.MirrorP", {"position": v(160.44, 128.48) * mm});
            skLineSegment(sketch, "E337.MirrorCS", {"start": v(171, 67.02) * mm, "end": v(171.01, 33.61) * mm});
            skPoint(sketch, "E338.MirrorP", {"position": v(176.75, 87.34) * mm});
            skLineSegment(sketch, "E339", {"start": v(141.01, 9.32) * mm, "end": v(142.61, 9.32) * mm});
            skLineSegment(sketch, "E340.MirrorCS", {"start": v(170.8, -16.91) * mm, "end": v(169.2, -16.92) * mm});
            skLineSegment(sketch, "E341.MirrorCS", {"start": v(170.76, 9.34) * mm, "end": v(169.16, 9.33) * mm});
            skLineSegment(sketch, "E342.MirrorCS", {"start": v(170.77, 0.21) * mm, "end": v(169.17, 0.2) * mm});
            skLineSegment(sketch, "E343.MirrorCS", {"start": v(170.78, -7.79) * mm, "end": v(169.18, -7.8) * mm});
            skLineSegment(sketch, "E344.MirrorCS", {"start": v(169.18, -7.8) * mm, "end": v(169.2, -16.92) * mm});
            skLineSegment(sketch, "E345.MirrorCS", {"start": v(170.77, 0.21) * mm, "end": v(170.76, 9.34) * mm});
            skLineSegment(sketch, "E346.MirrorCS", {"start": v(170.78, -7.79) * mm, "end": v(170.8, -16.91) * mm});
            skLineSegment(sketch, "E347.MirrorCS", {"start": v(169.17, 0.2) * mm, "end": v(169.16, 9.33) * mm});
            skSolve(sketch);
        }
        {
            var Q0;
            Q0=makeQuery(id+"F0.imprint","IMPRINT",FACE,{"disambiguationData":[TD([[makeQuery(id+"F0.imprint","IMPRINT",EDGE,{"derivedFrom":sQuery(id+"F0.wireOp",EDGE,"E5")}),-1.0]])]});
            var Q1;
            {var subQ11=sQuery(id+"F0.wireOp",EDGE,"E0.right");Q1=makeQuery(id+"F0.imprint","IMPRINT",FACE,{"disambiguationData":[TD([[makeQuery(id+"F0.imprint","IMPRINT",EDGE,{"derivedFrom":subQ11}),1.0]])]});}
            var Q2;
            Q2=makeQuery(id+"F0.imprint","IMPRINT",FACE,{"disambiguationData":[TD([[makeQuery(id+"F0.imprint","IMPRINT",EDGE,{"derivedFrom":sQuery(id+"F0.wireOp",EDGE,"E12.MirrorCS")}),1.0]])]});
            var Q3;
            Q3=makeQuery(id+"F0.imprint","IMPRINT",FACE,{"disambiguationData":[TD([[makeQuery(id+"F0.imprint","IMPRINT",EDGE,{"derivedFrom":sQuery(id+"F0.wireOp",EDGE,"E15.MirrorCS")}),-1.0]])]});
            var Q4;
            Q4=makeQuery(id+"F0.imprint","IMPRINT",FACE,{"disambiguationData":[TD([[makeQuery(id+"F0.imprint","IMPRINT",EDGE,{"derivedFrom":sQuery(id+"F0.wireOp",EDGE,"E0.bottom")}),-1.0]])]});
            var Q5;
            {var subQ0=sQuery(id+"F0.wireOp",EDGE,"E25");Q5=makeQuery(id+"F0.imprint","IMPRINT",FACE,{"disambiguationData":[TD([[makeQuery(id+"F0.imprint","IMPRINT",EDGE,{"derivedFrom":subQ0}),1.0]])]});}
            extrude(context, id + "F3", {"entities" : qUnion([Q0, Q1, Q2, Q3, Q4, Q5]), "depth" : 1.5 * mm, "offsetDistance" : 25.4 * mm});
        }
        {
            var Q0;
            Q0=qCreatedBy(makeId("Top.planeOp"),FACE);
            var sketch = newSketch(context, id + "F4", { "sketchPlane" : qUnion([Q0])});
            skLineSegment(sketch, "E348.bottom", {"start": v(9.33, 84.19) * mm, "end": v(11.33, 84.19) * mm});
            skLineSegment(sketch, "E348.top", {"start": v(9.33, 75.09) * mm, "end": v(11.33, 75.09) * mm});
            skLineSegment(sketch, "E348.left", {"start": v(9.33, 84.19) * mm, "end": v(9.33, 75.09) * mm});
            skLineSegment(sketch, "E348.right", {"start": v(11.33, 84.19) * mm, "end": v(11.33, 75.09) * mm});
            skLineSegment(sketch, "E349", {"start": v(11.33, 75.09) * mm, "end": v(11.33, 67.09) * mm});
            skLineSegment(sketch, "E350.top", {"start": v(9.33, 57.99) * mm, "end": v(11.33, 57.99) * mm});
            skLineSegment(sketch, "E350.right", {"start": v(11.33, 67.09) * mm, "end": v(11.33, 57.99) * mm});
            skLineSegment(sketch, "E351.left", {"start": v(11.33, 84.19) * mm, "end": v(11.33, 57.99) * mm});
            skArc(sketch, "E352", {"start": v(26.33, 77.15) * mm, "mid": v(24.77, 75.59) * mm, "end": v(26.33, 74.02) * mm});
            skArc(sketch, "E353", {"start": v(26.33, 68.28) * mm, "mid": v(24.77, 66.71) * mm, "end": v(26.33, 65.15) * mm});
            skArc(sketch, "E354", {"start": v(26.33, 72.65) * mm, "mid": v(24.77, 71.1) * mm, "end": v(26.33, 69.53) * mm});
            skLineSegment(sketch, "E355", {"start": v(26.33, 80) * mm, "end": v(26.33, 62.18) * mm});
            skPoint(sketch, "E351.right.end.orphan", {"position": v(41.33, 57.99) * mm});
            skPoint(sketch, "E356.orphan", {"position": v(41.33, 84.19) * mm});
            skPoint(sketch, "E357.0.midPoint", {"position": v(18.12, 75.89) * mm});
            skPoint(sketch, "E358.0.midPoint", {"position": v(18.12, 60.29) * mm});
            skPoint(sketch, "E359.0.midPoint", {"position": v(19.13, 68.84) * mm});
            skLineSegment(sketch, "E360.MirrorCS", {"start": v(41.33, 84.19) * mm, "end": v(41.33, 75.09) * mm});
            skLineSegment(sketch, "E361.MirrorCS", {"start": v(41.33, 67.09) * mm, "end": v(41.33, 57.99) * mm});
            skLineSegment(sketch, "E362.MirrorCS", {"start": v(41.33, 75.09) * mm, "end": v(41.33, 67.09) * mm});
            skLineSegment(sketch, "E363.MirrorCS", {"start": v(43.33, 67.09) * mm, "end": v(43.33, 57.99) * mm});
            skLineSegment(sketch, "E364.MirrorCS", {"start": v(43.33, 75.09) * mm, "end": v(41.33, 75.09) * mm});
            skLineSegment(sketch, "E365.MirrorCS", {"start": v(43.33, 84.19) * mm, "end": v(43.33, 75.09) * mm});
            skLineSegment(sketch, "E366.MirrorCS", {"start": v(41.33, 84.19) * mm, "end": v(41.33, 57.99) * mm});
            skArc(sketch, "E367.MirrorCS", {"start": v(26.33, 77.15) * mm, "mid": v(27.9, 75.59) * mm, "end": v(26.33, 74.02) * mm});
            skLineSegment(sketch, "E368.MirrorCS", {"start": v(43.33, 57.99) * mm, "end": v(41.33, 57.99) * mm});
            skLineSegment(sketch, "E369.MirrorCS", {"start": v(43.33, 84.19) * mm, "end": v(41.33, 84.19) * mm});
            skLineSegment(sketch, "E370.MirrorCS", {"start": v(43.33, 67.09) * mm, "end": v(41.33, 67.09) * mm});
            skArc(sketch, "E371.MirrorCS", {"start": v(26.33, 72.65) * mm, "mid": v(27.9, 71.1) * mm, "end": v(26.33, 69.53) * mm});
            skArc(sketch, "E372.MirrorCS", {"start": v(26.33, 68.28) * mm, "mid": v(27.9, 66.71) * mm, "end": v(26.33, 65.15) * mm});
            skLineSegment(sketch, "E373", {"start": v(11.33, 67.09) * mm, "end": v(9.33, 67.09) * mm});
            skLineSegment(sketch, "E374", {"start": v(9.33, 67.09) * mm, "end": v(9.33, 57.99) * mm});
            skPoint(sketch, "E375.orphan", {"position": v(9.33, 57.99) * mm});
            skPoint(sketch, "E376.orphan", {"position": v(26.33, 84.19) * mm});
            skPoint(sketch, "E377.orphan", {"position": v(26.33, 57.99) * mm});
            skArc(sketch, "E378", {"start": v(11.33, 84.19) * mm, "mid": v(26.33, 80.15) * mm, "end": v(41.33, 84.19) * mm});
            skLineSegment(sketch, "E379", {"start": v(11.33, 71.09) * mm, "end": v(41.33, 71.09) * mm});
            skArc(sketch, "E380.MirrorCS", {"start": v(11.33, 57.99) * mm, "mid": v(26.33, 62.03) * mm, "end": v(41.33, 57.99) * mm});
            skSolve(sketch);
        }
        {
            var Q0;
            {var subQ11=sQuery(id+"F4.wireOp",EDGE,"E348.right");Q0=makeQuery(id+"F4.imprint","IMPRINT",FACE,{"disambiguationData":[TD([[makeQuery(id+"F4.imprint","IMPRINT",EDGE,{"derivedFrom":subQ11}),1.0]])]});}
            var Q1;
            Q1=makeQuery(id+"F4.imprint","IMPRINT",FACE,{"disambiguationData":[TD([[makeQuery(id+"F4.imprint","IMPRINT",EDGE,{"derivedFrom":sQuery(id+"F4.wireOp",EDGE,"E353")}),-1.0]])]});
            var Q2;
            Q2=makeQuery(id+"F4.imprint","IMPRINT",FACE,{"disambiguationData":[TD([[makeQuery(id+"F4.imprint","IMPRINT",EDGE,{"derivedFrom":sQuery(id+"F4.wireOp",EDGE,"E363.MirrorCS")}),-1.0]])]});
            var Q3;
            Q3=makeQuery(id+"F4.imprint","IMPRINT",FACE,{"disambiguationData":[TD([[makeQuery(id+"F4.imprint","IMPRINT",EDGE,{"derivedFrom":sQuery(id+"F4.wireOp",EDGE,"E360.MirrorCS")}),1.0]])]});
            var Q4;
            Q4=makeQuery(id+"F4.imprint","IMPRINT",FACE,{"disambiguationData":[TD([[makeQuery(id+"F4.imprint","IMPRINT",EDGE,{"derivedFrom":sQuery(id+"F4.wireOp",EDGE,"E348.bottom")}),-1.0]])]});
            var Q5;
            {var subQ0=sQuery(id+"F4.wireOp",EDGE,"E373");Q5=makeQuery(id+"F4.imprint","IMPRINT",FACE,{"disambiguationData":[TD([[makeQuery(id+"F4.imprint","IMPRINT",EDGE,{"derivedFrom":subQ0}),1.0]])]});}
            extrude(context, id + "F5", {"entities" : qUnion([Q0, Q1, Q2, Q3, Q4, Q5]), "depth" : 2 * mm, "offsetDistance" : 25.4 * mm});
        }
        {
            var Q0;
            Q0=makeQuery(id+"F2.imprint","IMPRINT",FACE,{"disambiguationData":[TD([[makeQuery(id+"F2.imprint","IMPRINT",EDGE,{"derivedFrom":sQuery(id+"F2.wireOp",EDGE,"E243.MirrorCS")}),1.0]])]});
            extrude(context, id + "F6", {"entities" : qUnion([Q0]), "depth" : 2 * mm, "offsetDistance" : 25.4 * mm});
        }
        {
            var Q0;
            Q0=makeQuery(id+"F1.imprint","IMPRINT",FACE,{"disambiguationData":[TD([[makeQuery(id+"F1.imprint","IMPRINT",EDGE,{"derivedFrom":sQuery(id+"F1.wireOp",EDGE,"E34.MirrorCS")}),-1.0]])]});
            extrude(context, id + "F7", {"entities" : qUnion([Q0]), "depth" : 4 * mm, "offsetDistance" : 25.4 * mm});
        }
        {
            var Q0;
            Q0=qCreatedBy(makeId("Top.planeOp"),FACE);
            var sketch = newSketch(context, id + "F8", { "sketchPlane" : qUnion([Q0])});
            skCircle(sketch, "E381", {"center": v(54.6, -57.84) * mm, "radius": 1.3 * mm});
            skCircle(sketch, "E382", {"center": v(54.6, -57.84) * mm, "radius": 2 * mm});
            skSolve(sketch);
        }
        {
            var Q0;
            Q0=makeQuery(id+"F8.imprint","IMPRINT",FACE,{"disambiguationData":[TD([[makeQuery(id+"F8.imprint","IMPRINT",EDGE,{"derivedFrom":sQuery(id+"F8.wireOp",EDGE,"E381")}),-1.0]])]});
            extrude(context, id + "F9", {"entities" : qUnion([Q0]), "depth" : 30 * mm, "offsetDistance" : 25.4 * mm});
        }
        {
            var Q0;
            Q0=qCreatedBy(makeId("Top.planeOp"),FACE);
            var sketch = newSketch(context, id + "F10", { "sketchPlane" : qUnion([Q0])});
            skLineSegment(sketch, "E383.bottom", {"start": v(-164.62, 80.8) * mm, "end": v(-162.62, 80.8) * mm});
            skLineSegment(sketch, "E383.top", {"start": v(-164.62, 71.7) * mm, "end": v(-162.62, 71.7) * mm});
            skLineSegment(sketch, "E383.left", {"start": v(-164.62, 80.8) * mm, "end": v(-164.62, 71.7) * mm});
            skLineSegment(sketch, "E383.right", {"start": v(-162.62, 80.8) * mm, "end": v(-162.62, 71.7) * mm});
            skLineSegment(sketch, "E384", {"start": v(-162.62, 71.7) * mm, "end": v(-162.62, 63.7) * mm});
            skLineSegment(sketch, "E385.top", {"start": v(-164.62, 54.6) * mm, "end": v(-162.62, 54.6) * mm});
            skLineSegment(sketch, "E385.right", {"start": v(-162.62, 63.7) * mm, "end": v(-162.62, 54.6) * mm});
            skLineSegment(sketch, "E386.left", {"start": v(-162.62, 80.8) * mm, "end": v(-162.62, 54.6) * mm});
            skArc(sketch, "E387", {"start": v(-145.12, 73.76) * mm, "mid": v(-146.68, 72.2) * mm, "end": v(-145.12, 70.64) * mm});
            skArc(sketch, "E388", {"start": v(-145.12, 64.9) * mm, "mid": v(-146.68, 63.33) * mm, "end": v(-145.12, 61.77) * mm});
            skArc(sketch, "E389", {"start": v(-145.12, 69.27) * mm, "mid": v(-146.68, 67.7) * mm, "end": v(-145.12, 66.14) * mm});
            skLineSegment(sketch, "E390", {"start": v(-145.12, 76.61) * mm, "end": v(-145.12, 58.8) * mm});
            skPoint(sketch, "E386.right.end.orphan", {"position": v(-127.62, 54.6) * mm});
            skPoint(sketch, "E391.orphan", {"position": v(-127.62, 80.8) * mm});
            skPoint(sketch, "E392.0.midPoint", {"position": v(-155.83, 72.5) * mm});
            skPoint(sketch, "E393.0.midPoint", {"position": v(-155.83, 56.9) * mm});
            skPoint(sketch, "E394.0.midPoint", {"position": v(-154.82, 65.45) * mm});
            skLineSegment(sketch, "E395.MirrorCS", {"start": v(-127.62, 80.8) * mm, "end": v(-127.62, 71.7) * mm});
            skLineSegment(sketch, "E396.MirrorCS", {"start": v(-127.62, 63.7) * mm, "end": v(-127.62, 54.6) * mm});
            skLineSegment(sketch, "E397.MirrorCS", {"start": v(-127.62, 71.7) * mm, "end": v(-127.62, 63.7) * mm});
            skLineSegment(sketch, "E398.MirrorCS", {"start": v(-125.62, 63.7) * mm, "end": v(-125.62, 54.6) * mm});
            skLineSegment(sketch, "E399.MirrorCS", {"start": v(-125.62, 71.7) * mm, "end": v(-127.62, 71.7) * mm});
            skLineSegment(sketch, "E400.MirrorCS", {"start": v(-125.62, 80.8) * mm, "end": v(-125.62, 71.7) * mm});
            skLineSegment(sketch, "E401.MirrorCS", {"start": v(-127.62, 80.8) * mm, "end": v(-127.62, 54.6) * mm});
            skArc(sketch, "E402.MirrorCS", {"start": v(-145.12, 73.76) * mm, "mid": v(-143.56, 72.2) * mm, "end": v(-145.12, 70.64) * mm});
            skLineSegment(sketch, "E403.MirrorCS", {"start": v(-125.62, 54.6) * mm, "end": v(-127.62, 54.6) * mm});
            skLineSegment(sketch, "E404.MirrorCS", {"start": v(-125.62, 80.8) * mm, "end": v(-127.62, 80.8) * mm});
            skLineSegment(sketch, "E405.MirrorCS", {"start": v(-125.62, 63.7) * mm, "end": v(-127.62, 63.7) * mm});
            skArc(sketch, "E406.MirrorCS", {"start": v(-145.12, 69.27) * mm, "mid": v(-143.56, 67.7) * mm, "end": v(-145.12, 66.14) * mm});
            skArc(sketch, "E407.MirrorCS", {"start": v(-145.12, 64.9) * mm, "mid": v(-143.56, 63.33) * mm, "end": v(-145.12, 61.77) * mm});
            skLineSegment(sketch, "E408", {"start": v(-162.62, 63.7) * mm, "end": v(-164.62, 63.7) * mm});
            skLineSegment(sketch, "E409", {"start": v(-164.62, 63.7) * mm, "end": v(-164.62, 54.6) * mm});
            skPoint(sketch, "E410.orphan", {"position": v(-164.62, 54.6) * mm});
            skPoint(sketch, "E411.orphan", {"position": v(-145.12, 80.8) * mm});
            skPoint(sketch, "E412.orphan", {"position": v(-145.12, 54.6) * mm});
            skLineSegment(sketch, "E413", {"start": v(-162.62, 67.7) * mm, "end": v(-127.62, 67.7) * mm});
            skArc(sketch, "E414", {"start": v(-162.62, 80.8) * mm, "mid": v(-145.12, 76.45) * mm, "end": v(-127.62, 80.8) * mm});
            skArc(sketch, "E415", {"start": v(-127.62, 54.6) * mm, "mid": v(-145.12, 58.98) * mm, "end": v(-162.62, 54.6) * mm});
            skSolve(sketch);
        }
        {
            var Q0;
            {var subQ1=sQuery(id+"F10.wireOp",EDGE,"E395.MirrorCS");Q0=makeQuery(id+"F10.imprint","IMPRINT",FACE,{"disambiguationData":[TD([[makeQuery(id+"F10.imprint","IMPRINT",EDGE,{"derivedFrom":subQ1}),-1.0]])]});}
            var Q1;
            Q1=makeQuery(id+"F10.imprint","IMPRINT",FACE,{"disambiguationData":[TD([[makeQuery(id+"F10.imprint","IMPRINT",EDGE,{"derivedFrom":sQuery(id+"F10.wireOp",EDGE,"E383.bottom")}),-1.0]])]});
            var Q2;
            {var subQ7=sQuery(id+"F10.wireOp",EDGE,"E383.right");Q2=makeQuery(id+"F10.imprint","IMPRINT",FACE,{"disambiguationData":[TD([[makeQuery(id+"F10.imprint","IMPRINT",EDGE,{"derivedFrom":subQ7}),1.0]])]});}
            var Q3;
            {var subQ5=sQuery(id+"F10.wireOp",EDGE,"E407.MirrorCS");Q3=makeQuery(id+"F10.imprint","IMPRINT",FACE,{"disambiguationData":[TD([[makeQuery(id+"F10.imprint","IMPRINT",EDGE,{"derivedFrom":subQ5}),1.0]])]});}
            var Q4;
            Q4=makeQuery(id+"F10.imprint","IMPRINT",FACE,{"disambiguationData":[TD([[makeQuery(id+"F10.imprint","IMPRINT",EDGE,{"derivedFrom":sQuery(id+"F10.wireOp",EDGE,"E398.MirrorCS")}),-1.0]])]});
            var Q5;
            Q5=makeQuery(id+"F10.imprint","IMPRINT",FACE,{"disambiguationData":[TD([[makeQuery(id+"F10.imprint","IMPRINT",EDGE,{"derivedFrom":sQuery(id+"F10.wireOp",EDGE,"E395.MirrorCS")}),1.0]])]});
            var Q6;
            {var subQ0=sQuery(id+"F10.wireOp",EDGE,"E408");Q6=makeQuery(id+"F10.imprint","IMPRINT",FACE,{"disambiguationData":[TD([[makeQuery(id+"F10.imprint","IMPRINT",EDGE,{"derivedFrom":subQ0}),1.0]])]});}
            var Q7;
            {var subQ0=sQuery(id+"F10.wireOp",EDGE,"E388");Q7=makeQuery(id+"F10.imprint","IMPRINT",FACE,{"disambiguationData":[TD([[makeQuery(id+"F10.imprint","IMPRINT",EDGE,{"derivedFrom":subQ0}),-1.0]])]});}
            extrude(context, id + "F11", {"entities" : qUnion([Q0, Q1, Q2, Q3, Q4, Q5, Q6, Q7]), "depth" : 1.5 * mm, "offsetDistance" : 25.4 * mm});
        }
        {
            var Q0;
            Q0=qCreatedBy(makeId("Top.planeOp"),FACE);
            var sketch = newSketch(context, id + "F12", { "sketchPlane" : qUnion([Q0])});
            skLineSegment(sketch, "E416.bottom", {"start": v(-184.97, 33.87) * mm, "end": v(-182.97, 33.87) * mm});
            skLineSegment(sketch, "E416.top", {"start": v(-184.97, 24.77) * mm, "end": v(-182.97, 24.77) * mm});
            skLineSegment(sketch, "E416.left", {"start": v(-184.97, 33.87) * mm, "end": v(-184.97, 24.77) * mm});
            skLineSegment(sketch, "E416.right", {"start": v(-182.97, 33.87) * mm, "end": v(-182.97, 24.77) * mm});
            skLineSegment(sketch, "E417", {"start": v(-182.97, 24.77) * mm, "end": v(-182.97, 16.77) * mm});
            skLineSegment(sketch, "E418.top", {"start": v(-184.97, 7.67) * mm, "end": v(-182.97, 7.67) * mm});
            skLineSegment(sketch, "E418.right", {"start": v(-182.97, 16.77) * mm, "end": v(-182.97, 7.67) * mm});
            skLineSegment(sketch, "E419.left", {"start": v(-182.97, 33.87) * mm, "end": v(-182.97, 7.67) * mm});
            skArc(sketch, "E420", {"start": v(-165.47, 26.83) * mm, "mid": v(-167.03, 25.27) * mm, "end": v(-165.47, 23.7) * mm});
            skArc(sketch, "E421", {"start": v(-165.47, 17.96) * mm, "mid": v(-167.03, 16.4) * mm, "end": v(-165.47, 14.83) * mm});
            skArc(sketch, "E422", {"start": v(-165.47, 22.33) * mm, "mid": v(-167.03, 20.77) * mm, "end": v(-165.47, 19.2) * mm});
            skLineSegment(sketch, "E423", {"start": v(-165.47, 29.68) * mm, "end": v(-165.47, 11.86) * mm});
            skPoint(sketch, "E419.right.end.orphan", {"position": v(-147.97, 7.67) * mm});
            skPoint(sketch, "E424.orphan", {"position": v(-147.97, 33.87) * mm});
            skPoint(sketch, "E425.0.midPoint", {"position": v(-176.18, 25.57) * mm});
            skPoint(sketch, "E426.0.midPoint", {"position": v(-176.18, 9.97) * mm});
            skPoint(sketch, "E427.0.midPoint", {"position": v(-175.17, 18.52) * mm});
            skLineSegment(sketch, "E428.MirrorCS", {"start": v(-147.97, 33.87) * mm, "end": v(-147.97, 24.77) * mm});
            skLineSegment(sketch, "E429.MirrorCS", {"start": v(-147.97, 16.77) * mm, "end": v(-147.97, 7.67) * mm});
            skLineSegment(sketch, "E430.MirrorCS", {"start": v(-147.97, 24.77) * mm, "end": v(-147.97, 16.77) * mm});
            skLineSegment(sketch, "E431.MirrorCS", {"start": v(-145.97, 16.77) * mm, "end": v(-145.97, 7.67) * mm});
            skLineSegment(sketch, "E432.MirrorCS", {"start": v(-145.97, 24.77) * mm, "end": v(-147.97, 24.77) * mm});
            skLineSegment(sketch, "E433.MirrorCS", {"start": v(-145.97, 33.87) * mm, "end": v(-145.97, 24.77) * mm});
            skLineSegment(sketch, "E434.MirrorCS", {"start": v(-147.97, 33.87) * mm, "end": v(-147.97, 7.67) * mm});
            skArc(sketch, "E435.MirrorCS", {"start": v(-165.47, 26.83) * mm, "mid": v(-163.9, 25.27) * mm, "end": v(-165.47, 23.7) * mm});
            skLineSegment(sketch, "E436.MirrorCS", {"start": v(-145.97, 7.67) * mm, "end": v(-147.97, 7.67) * mm});
            skLineSegment(sketch, "E437.MirrorCS", {"start": v(-145.97, 33.87) * mm, "end": v(-147.97, 33.87) * mm});
            skLineSegment(sketch, "E438.MirrorCS", {"start": v(-145.97, 16.77) * mm, "end": v(-147.97, 16.77) * mm});
            skArc(sketch, "E439.MirrorCS", {"start": v(-165.47, 22.33) * mm, "mid": v(-163.9, 20.77) * mm, "end": v(-165.47, 19.2) * mm});
            skArc(sketch, "E440.MirrorCS", {"start": v(-165.47, 17.96) * mm, "mid": v(-163.9, 16.4) * mm, "end": v(-165.47, 14.83) * mm});
            skLineSegment(sketch, "E441", {"start": v(-182.97, 16.77) * mm, "end": v(-184.97, 16.77) * mm});
            skLineSegment(sketch, "E442", {"start": v(-184.97, 16.77) * mm, "end": v(-184.97, 7.67) * mm});
            skPoint(sketch, "E443.orphan", {"position": v(-184.97, 7.67) * mm});
            skPoint(sketch, "E444.orphan", {"position": v(-165.47, 33.87) * mm});
            skPoint(sketch, "E445.orphan", {"position": v(-165.47, 7.67) * mm});
            skLineSegment(sketch, "E446", {"start": v(-182.97, 20.77) * mm, "end": v(-147.97, 20.77) * mm});
            skArc(sketch, "E447", {"start": v(-182.97, 33.87) * mm, "mid": v(-165.47, 29.52) * mm, "end": v(-147.97, 33.87) * mm});
            skArc(sketch, "E448", {"start": v(-147.97, 7.67) * mm, "mid": v(-165.47, 12.05) * mm, "end": v(-182.97, 7.67) * mm});
            skSolve(sketch);
        }
        {
            var Q0;
            {var subQ1=sQuery(id+"F12.wireOp",EDGE,"E428.MirrorCS");Q0=makeQuery(id+"F12.imprint","IMPRINT",FACE,{"disambiguationData":[TD([[makeQuery(id+"F12.imprint","IMPRINT",EDGE,{"derivedFrom":subQ1}),-1.0]])]});}
            var Q1;
            {var subQ7=sQuery(id+"F12.wireOp",EDGE,"E416.right");Q1=makeQuery(id+"F12.imprint","IMPRINT",FACE,{"disambiguationData":[TD([[makeQuery(id+"F12.imprint","IMPRINT",EDGE,{"derivedFrom":subQ7}),1.0]])]});}
            var Q2;
            {var subQ0=sQuery(id+"F12.wireOp",EDGE,"E421");Q2=makeQuery(id+"F12.imprint","IMPRINT",FACE,{"disambiguationData":[TD([[makeQuery(id+"F12.imprint","IMPRINT",EDGE,{"derivedFrom":subQ0}),-1.0]])]});}
            var Q3;
            {var subQ0=sQuery(id+"F12.wireOp",EDGE,"E441");Q3=makeQuery(id+"F12.imprint","IMPRINT",FACE,{"disambiguationData":[TD([[makeQuery(id+"F12.imprint","IMPRINT",EDGE,{"derivedFrom":subQ0}),1.0]])]});}
            var Q4;
            Q4=makeQuery(id+"F12.imprint","IMPRINT",FACE,{"disambiguationData":[TD([[makeQuery(id+"F12.imprint","IMPRINT",EDGE,{"derivedFrom":sQuery(id+"F12.wireOp",EDGE,"E431.MirrorCS")}),-1.0]])]});
            var Q5;
            Q5=makeQuery(id+"F12.imprint","IMPRINT",FACE,{"disambiguationData":[TD([[makeQuery(id+"F12.imprint","IMPRINT",EDGE,{"derivedFrom":sQuery(id+"F12.wireOp",EDGE,"E428.MirrorCS")}),1.0]])]});
            var Q6;
            Q6=makeQuery(id+"F12.imprint","IMPRINT",FACE,{"disambiguationData":[TD([[makeQuery(id+"F12.imprint","IMPRINT",EDGE,{"derivedFrom":sQuery(id+"F12.wireOp",EDGE,"E416.bottom")}),-1.0]])]});
            var Q7;
            {var subQ5=sQuery(id+"F12.wireOp",EDGE,"E440.MirrorCS");Q7=makeQuery(id+"F12.imprint","IMPRINT",FACE,{"disambiguationData":[TD([[makeQuery(id+"F12.imprint","IMPRINT",EDGE,{"derivedFrom":subQ5}),1.0]])]});}
            extrude(context, id + "F13", {"entities" : qUnion([Q0, Q1, Q2, Q3, Q4, Q5, Q6, Q7]), "depth" : 1.5 * mm, "offsetDistance" : 25.4 * mm});
        }
    });
